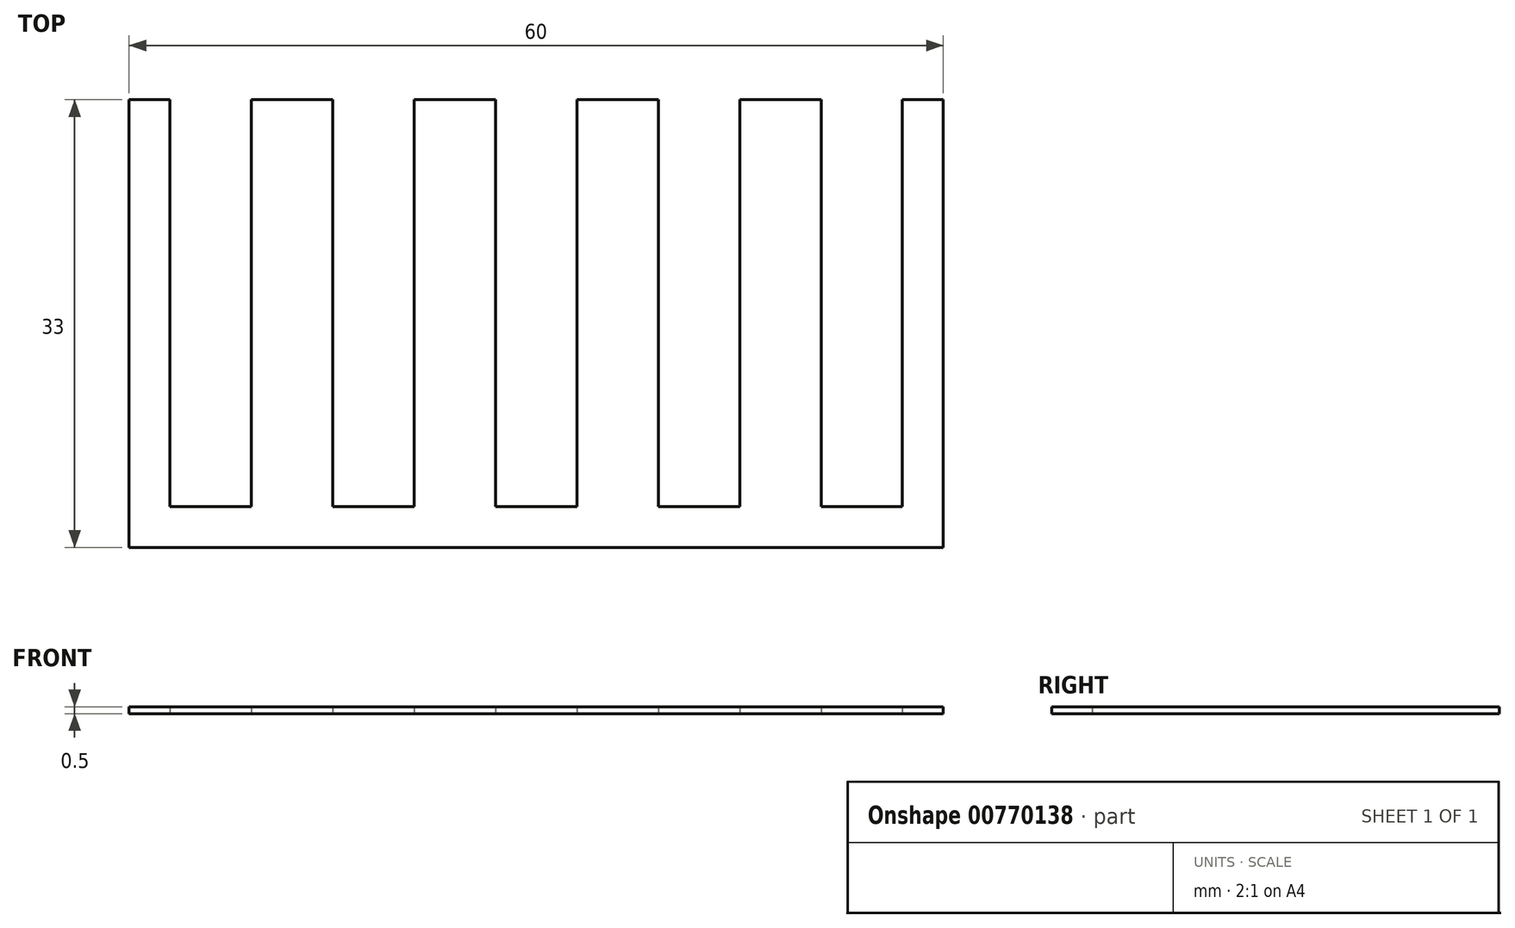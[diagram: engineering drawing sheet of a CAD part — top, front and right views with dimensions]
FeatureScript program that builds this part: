
annotation { "Feature Type Name" : "Feature", "Feature Type Description" : "" }
export const myFeature = defineFeature(function(context is Context, id is Id, definition is map)
    precondition{}
    {
        {
            var Q0;
            Q0=qCreatedBy(makeId("Top.planeOp"),FACE);
            var sketch = newSketch(context, id + "F0", { "sketchPlane" : qUnion([Q0])});
            skPoint(sketch, "E0.middle", {"position": v(0, 0) * mm});
            skLineSegment(sketch, "E1.top", {"start": v(-3, -10) * mm, "end": v(3, -10) * mm});
            skLineSegment(sketch, "E1.left", {"start": v(-3, 20) * mm, "end": v(-3, -10) * mm});
            skLineSegment(sketch, "E1.right", {"start": v(3, 20) * mm, "end": v(3, -10) * mm});
            skLineSegment(sketch, "E2.1.0.0", {"start": v(9, 20) * mm, "end": v(9, -10) * mm});
            skLineSegment(sketch, "E2.1.0.1", {"start": v(9, -10) * mm, "end": v(15, -10) * mm});
            skLineSegment(sketch, "E2.1.0.2", {"start": v(15, 20) * mm, "end": v(15, -10) * mm});
            skLineSegment(sketch, "E2.2.0.0", {"start": v(21, 20) * mm, "end": v(21, -10) * mm});
            skLineSegment(sketch, "E2.2.0.1", {"start": v(21, -10) * mm, "end": v(27, -10) * mm});
            skLineSegment(sketch, "E2.2.0.2", {"start": v(27, 20) * mm, "end": v(27, -10) * mm});
            skLineSegment(sketch, "E3.MirrorCS", {"start": v(-9, 20) * mm, "end": v(-9, -10) * mm});
            skLineSegment(sketch, "E4.MirrorCS", {"start": v(-9, -10) * mm, "end": v(-15, -10) * mm});
            skLineSegment(sketch, "E5.MirrorCS", {"start": v(-15, 20) * mm, "end": v(-15, -10) * mm});
            skLineSegment(sketch, "E6.MirrorCS", {"start": v(-21, 20) * mm, "end": v(-21, -10) * mm});
            skLineSegment(sketch, "E7.MirrorCS", {"start": v(-21, -10) * mm, "end": v(-27, -10) * mm});
            skLineSegment(sketch, "E8.MirrorCS", {"start": v(-27, 20) * mm, "end": v(-27, -10) * mm});
            skLineSegment(sketch, "E9", {"start": v(-30, 20) * mm, "end": v(-27, 20) * mm});
            skLineSegment(sketch, "E10", {"start": v(-21, 20) * mm, "end": v(-15, 20) * mm});
            skLineSegment(sketch, "E11", {"start": v(-9, 20) * mm, "end": v(-3, 20) * mm});
            skLineSegment(sketch, "E12", {"start": v(3, 20) * mm, "end": v(9, 20) * mm});
            skLineSegment(sketch, "E13", {"start": v(15, 20) * mm, "end": v(21, 20) * mm});
            skLineSegment(sketch, "E14", {"start": v(27, 20) * mm, "end": v(30, 20) * mm});
            skLineSegment(sketch, "E15", {"start": v(-30, 20) * mm, "end": v(-30, -13) * mm});
            skLineSegment(sketch, "E16", {"start": v(30, 20) * mm, "end": v(30, -13) * mm});
            skLineSegment(sketch, "E17", {"start": v(-30, -13) * mm, "end": v(30, -13) * mm});
            skSolve(sketch);
        }
        {
            var Q0;
            Q0=makeQuery(id+"F0.imprint","IMPRINT",FACE,{"disambiguationData":[TD([[makeQuery(id+"F0.imprint","IMPRINT",EDGE,{"derivedFrom":sQuery(id+"F0.wireOp",EDGE,"E1.top")}),-1.0]])]});
            extrude(context, id + "F1", {"entities" : qUnion([Q0]), "depth" : .5 * mm, "offsetDistance" : 25 * mm});
        }
    });
